# Revit family: QF_MACOM_RPTx-AITM
name_source: partatom
category: Equipamento especial
units: mm (PartAtom-declared; Revit-internal decimal feet)

## family parameters
Com base no plano de trabalho = Não
Compartilhado = Não
Corte com vazios quando carregada = Não
Cota do conector redondo = Utilizar diâmetro
Número OmniClass = 23.40.40.11.11.11
Ponto de cálculo do ambiente = Não
Sempre na vertical = Sim
Tipo de parte = Normal
Título OmniClass = Refrigerators

## types (3) — shared parameters
Elevação padrão = 0 mm
Fabricante = MACOM
URL = https://www.acosmacom.com.br
Work Temperature (Cabeçotel) = +1ºC a +5ºC
Work Temperature (Gabinete) = +1ºC a +4ºC

## per-type parameters (varying)
| type | Center Handle | Defrost Power | Descrição | Door 1 | Door 2 | Door 3 | Door Separator | GN's Capacity (1/6-150) | Handle Center | Length Actual | Number of Doors | Separate Door Location | Volume |
| RPT3-AITM | 985 mm | 686 W | REFRIG. HORIZ PREP TABLE MACOM, MEGA P/ 27 GNS 1/6-150, 3 PORTAS INOX, 24 TRILHOS, ALTILENO-1967X800X900 | 529 mm | Sim | Sim | 800 mm | 27 | Não | 1970 mm | 3 | 1012 mm | 1,54 m³ |
| RPT2-AITM | 720 mm | 624 W | REFRIG HORIZ PREP TABLE MACOM, MEGA P/ 21 GNS 1/6-150, 2 PORTAS INOX, 16 TRILHOS, ALTILENO-1435X800X900 | 529 mm | Sim | Não | 10 mm | 21 | Sim | 1439 mm | 2 | 720 mm | 1,12 m³ |
| RPT1-AITM | 454 mm | 321 W | REFRIG HORIZ PREP TABLE MACOM, MEGA TOP- 908X838X922 | 0 mm | Não | Não | 10 mm | 12 | Sim | 908 mm | 1 | 454 mm | 0,70 m³ |

note: column(s) folded — value = type name in every type: Modelo

## geometry (parser evidence)
native form markers: Sweep x4
no freeform markers — native parametric forms only
